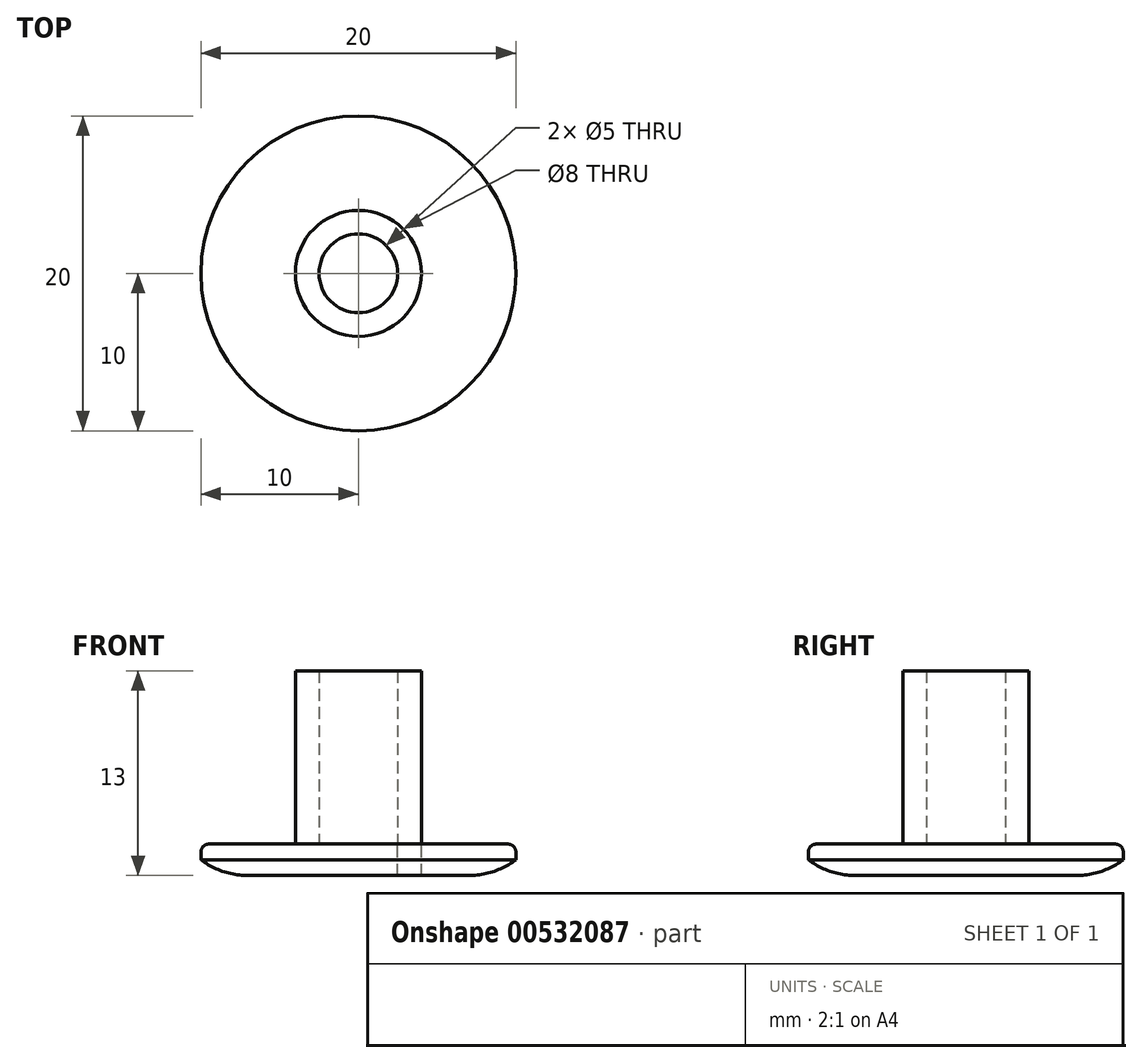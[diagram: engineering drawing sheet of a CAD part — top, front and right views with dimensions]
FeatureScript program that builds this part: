
annotation { "Feature Type Name" : "Feature", "Feature Type Description" : "" }
export const myFeature = defineFeature(function(context is Context, id is Id, definition is map)
    precondition{}
    {
        {
            var Q0;
            Q0=qCreatedBy(makeId("Top.planeOp"),FACE);
            var sketch = newSketch(context, id + "F0", { "sketchPlane" : qUnion([Q0])});
            skCircle(sketch, "E0", {"center": v(0, 0) * mm, "radius": 4 * mm});
            skCircle(sketch, "E1", {"center": v(0, 0) * mm, "radius": 10 * mm});
            skCircle(sketch, "E2", {"center": v(0, 0) * mm, "radius": 2.5 * mm});
            skSolve(sketch);
        }
        {
            var Q0;
            Q0 = qSketchRegion(id + "F0", true);
            extrude(context, id + "F1", {"entities" : qUnion([Q0]), "oppositeDirection" : true, "depth" : 2 * mm, "offsetDistance" : 25 * mm});
        }
        {
            var Q0;
            Q0=makeQuery(id+"F0.imprint","IMPRINT",FACE,{"disambiguationData":[TD([[makeQuery(id+"F0.imprint","IMPRINT",EDGE,{"derivedFrom":sQuery(id+"F0.wireOp",EDGE,"E0")}),1.0]])]});
            extrude(context, id + "F2", {"entities" : qUnion([Q0]), "operationType" : NewBodyOperationType.ADD, "depth" : 11 * mm, "offsetDistance" : 25 * mm});
        }
        {
            var Q0;
            Q0=makeQuery(id+"F1.opExtrude","CAP_EDGE",EDGE,{"disambiguationData":[OSD([sQuery(id+"F0.wireOp",EDGE,"E1")])],"isStart":true});
            fillet(context, id + "F3", {"entities" : qUnion([Q0]), "radius" : 0.5 * mm, "tangentPropagation" : true, "allowEdgeOverflow" : false});
        }
        {
            var Q0;
            Q0=makeQuery(id+"F0.imprint","IMPRINT",FACE,{"disambiguationData":[TD([[makeQuery(id+"F0.imprint","IMPRINT",EDGE,{"derivedFrom":sQuery(id+"F0.wireOp",EDGE,"E0")}),1.0]])]});
            extrude(context, id + "F4", {"entities" : qUnion([Q0]), "oppositeDirection" : true, "depth" : 2 * mm, "offsetDistance" : 25 * mm});
        }
        {
            var Q0;
            Q0=makeQuery(id+"F1.opExtrude","CAP_EDGE",EDGE,{"disambiguationData":[OSD([sQuery(id+"F0.wireOp",EDGE,"E1")])],"isStart":false});
            chamfer(context, id + "F5", {"entities" : qUnion([Q0]), "width" : 1 * mm, "tangentPropagation" : true});
        }
        {
            var Q0;
            {var subQ0=sQuery(id+"F0.wireOp",EDGE,"E1");Q0=makeQuery(id+"F5.opChamfer","BLEND_EDGE",EDGE,{"blendedFrom":[makeQuery(id+"F1.opExtrude","CAP_EDGE",EDGE,{"disambiguationData":[OSD([subQ0])],"isStart":false}),makeQuery(id+"F1.opExtrude","CAP_FACE",FACE,{"disambiguationData":[OSD([sQuery(id+"F0.wireOp",EDGE,"E0"),subQ0])],"isStart":false})],"blendedInto":[makeQuery(id+"F1.opExtrude","CAP_FACE",FACE,{"disambiguationData":[OSD([sQuery(id+"F0.wireOp",EDGE,"E0"),subQ0])],"isStart":false})]});}
            fillet(context, id + "F6", {"entities" : qUnion([Q0]), "radius" : 5 * mm, "tangentPropagation" : true, "allowEdgeOverflow" : false});
        }
    });
